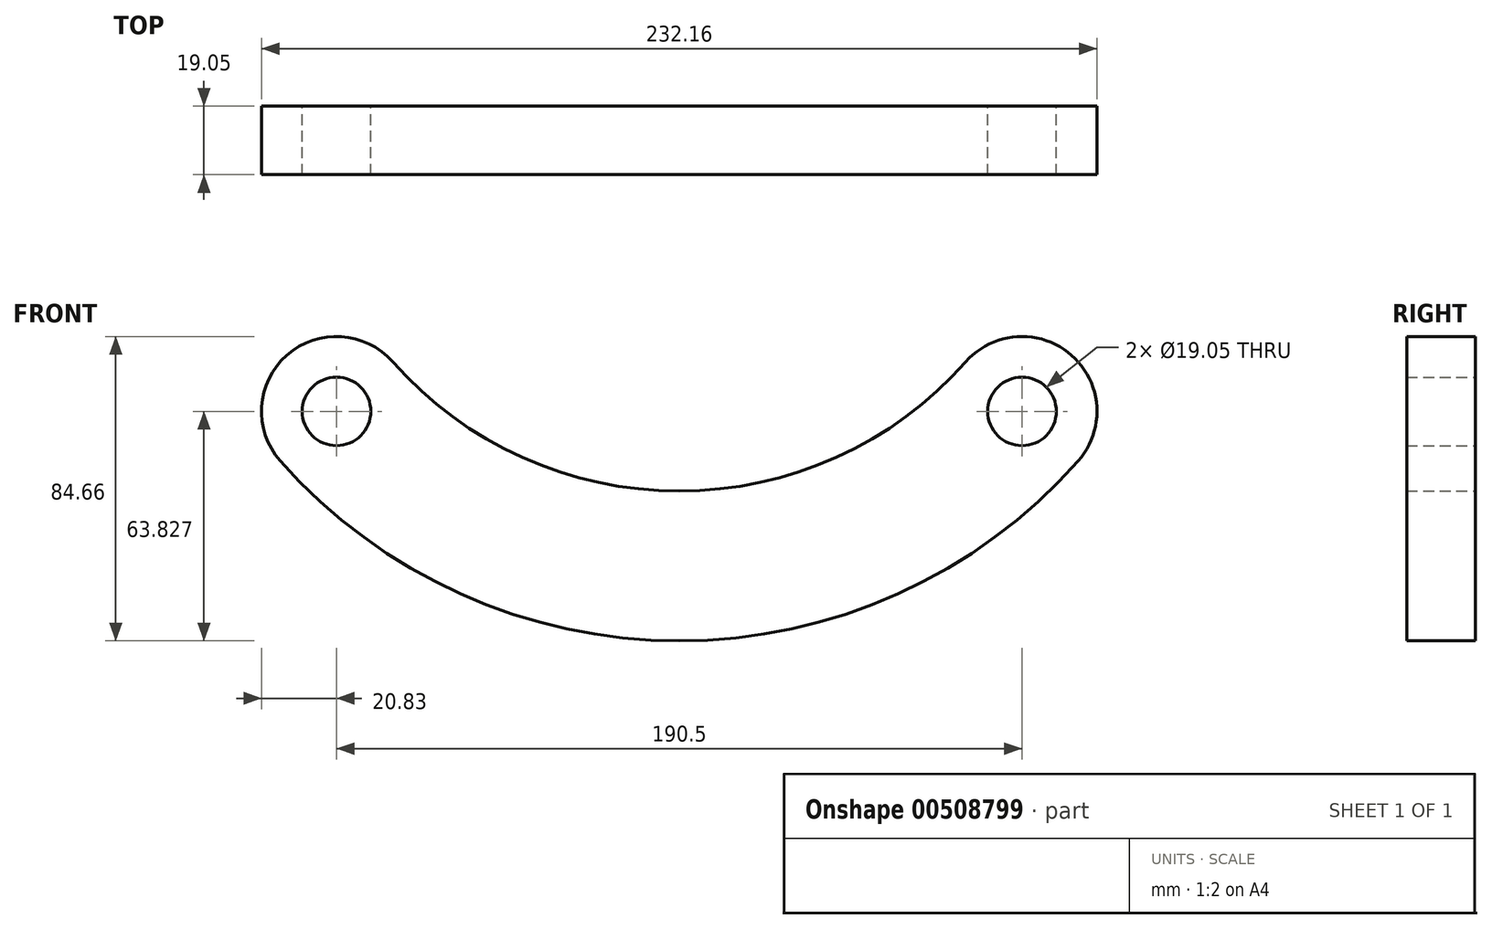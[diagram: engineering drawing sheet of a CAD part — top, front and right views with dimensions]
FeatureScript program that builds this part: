
annotation { "Feature Type Name" : "Feature", "Feature Type Description" : "" }
export const myFeature = defineFeature(function(context is Context, id is Id, definition is map)
    precondition{}
    {
        {
            var Q0;
            Q0=qCreatedBy(makeId("Front.planeOp"),FACE);
            var sketch = newSketch(context, id + "F0", { "sketchPlane" : qUnion([Q0])});
            skLineSegment(sketch, "E0", {"start": v(-95.25, 0) * mm, "end": v(95.25, 0) * mm, "construction": true});
            skLineSegment(sketch, "E1", {"start": v(-95.25, 0) * mm, "end": v(-95.25, 43) * mm, "construction": true});
            skLineSegment(sketch, "E2", {"start": v(95.25, 0) * mm, "end": v(95.25, 43) * mm, "construction": true});
            skCircle(sketch, "E3", {"center": v(-95.25, 43) * mm, "radius": 9.53 * mm});
            skCircle(sketch, "E4", {"center": v(95.25, 43) * mm, "radius": 9.53 * mm});
            skArc(sketch, "E5", {"start": v(-95.25, 43) * mm, "mid": v(0, 0) * mm, "end": v(95.25, 43) * mm, "construction": true});
            skArc(sketch, "E6.0", {"start": v(-110.87, 29.22) * mm, "mid": v(0, -20.83) * mm, "end": v(110.87, 29.22) * mm});
            skArc(sketch, "E7.0", {"start": v(-79.63, 56.77) * mm, "mid": v(0, 20.83) * mm, "end": v(79.63, 56.77) * mm});
            skArc(sketch, "E8", {"start": v(-79.63, 56.77) * mm, "mid": v(-109.03, 58.62) * mm, "end": v(-110.87, 29.22) * mm});
            skArc(sketch, "E9", {"start": v(110.87, 29.22) * mm, "mid": v(109.03, 58.62) * mm, "end": v(79.63, 56.77) * mm});
            skSolve(sketch);
        }
        {
            var Q0;
            Q0=makeQuery(id+"F0.imprint","IMPRINT",FACE,{"disambiguationData":[TD([[makeQuery(id+"F0.imprint","IMPRINT",EDGE,{"derivedFrom":sQuery(id+"F0.wireOp",EDGE,"E3")}),-1.0]])]});
            extrude(context, id + "F1", {"entities" : qUnion([Q0]), "depth" : 19.05 * mm});
        }
    });
